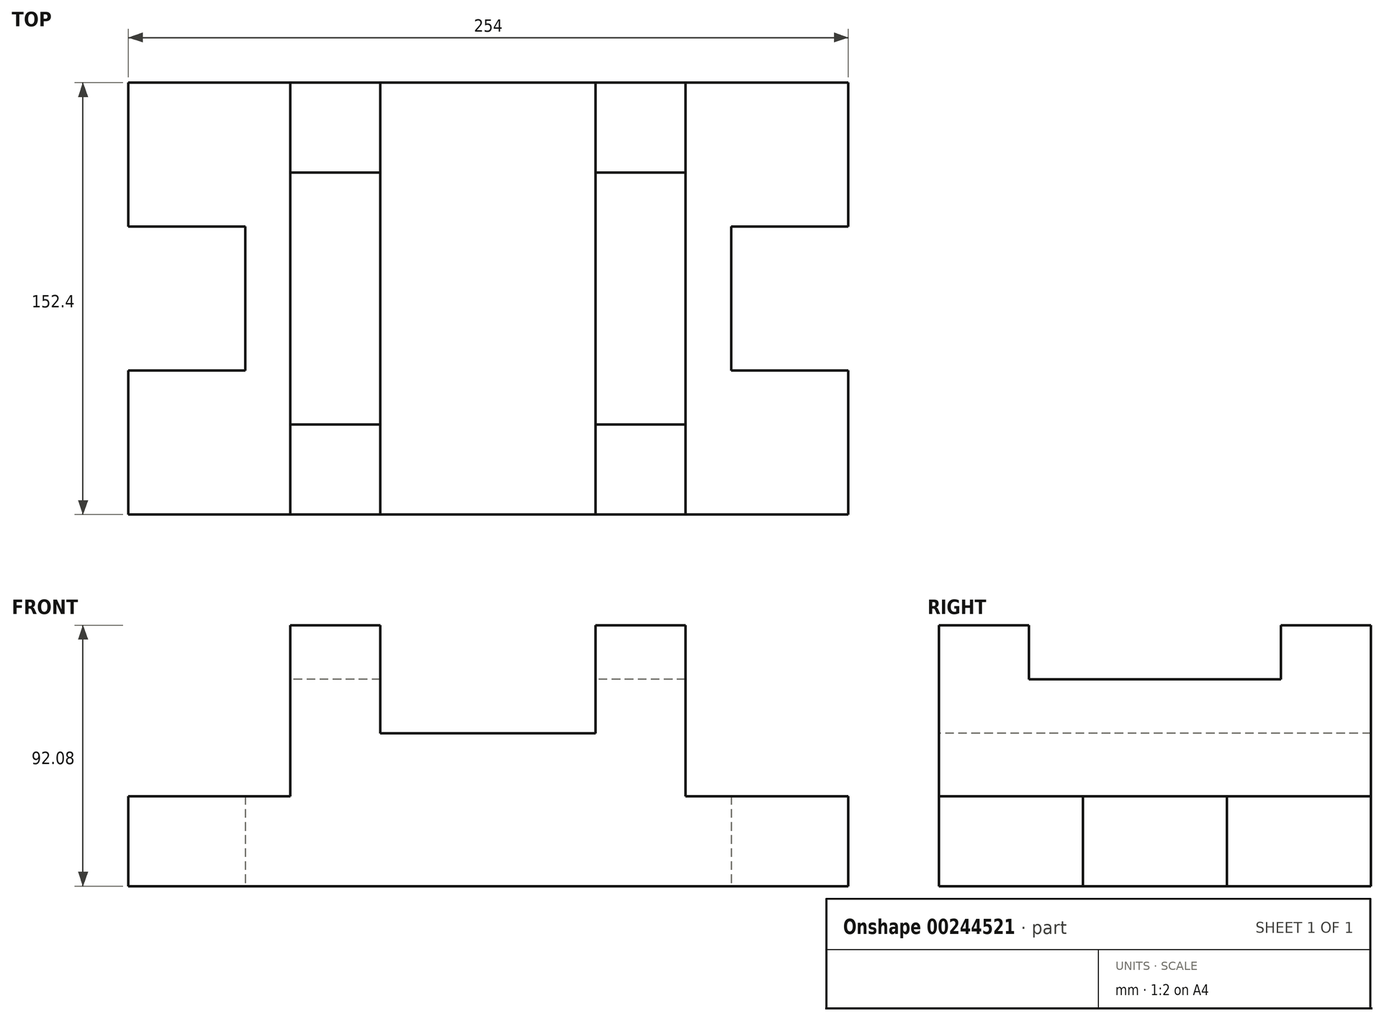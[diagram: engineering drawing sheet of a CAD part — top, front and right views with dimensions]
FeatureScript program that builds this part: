
annotation { "Feature Type Name" : "Feature", "Feature Type Description" : "" }
export const myFeature = defineFeature(function(context is Context, id is Id, definition is map)
    precondition{}
    {
        {
            var Q0;
            Q0=qCreatedBy(makeId("Top.planeOp"),FACE);
            var sketch = newSketch(context, id + "F0", { "sketchPlane" : qUnion([Q0])});
            skLineSegment(sketch, "E0.bottom", {"start": v(127, 76.2) * mm, "end": v(-127, 76.2) * mm});
            skLineSegment(sketch, "E0.top", {"start": v(127, -76.2) * mm, "end": v(-127, -76.2) * mm});
            skLineSegment(sketch, "E0.left", {"start": v(127, 76.2) * mm, "end": v(127, 25.4) * mm});
            skLineSegment(sketch, "E0.right", {"start": v(-127, 76.2) * mm, "end": v(-127, 25.4) * mm});
            skPoint(sketch, "E0.middle", {"position": v(0, 0) * mm});
            skLineSegment(sketch, "E1", {"start": v(-69.85, -76.2) * mm, "end": v(-69.85, 76.2) * mm});
            skLineSegment(sketch, "E2", {"start": v(69.54, -76.2) * mm, "end": v(69.54, 76.2) * mm});
            skLineSegment(sketch, "E3", {"start": v(-38.1, 76.2) * mm, "end": v(-38.1, -76.2) * mm});
            skLineSegment(sketch, "E4", {"start": v(37.8, 76.2) * mm, "end": v(37.8, -76.2) * mm});
            skLineSegment(sketch, "E5", {"start": v(-38.1, 44.45) * mm, "end": v(-69.85, 44.45) * mm});
            skLineSegment(sketch, "E6", {"start": v(69.54, 44.45) * mm, "end": v(37.8, 44.45) * mm});
            skLineSegment(sketch, "E7", {"start": v(-38.1, -44.45) * mm, "end": v(-69.85, -44.45) * mm});
            skLineSegment(sketch, "E8", {"start": v(69.54, -44.45) * mm, "end": v(37.8, -44.45) * mm});
            skPoint(sketch, "E9.middle", {"position": v(-127, 0) * mm});
            skLineSegment(sketch, "E10.right", {"start": v(85.72, 25.4) * mm, "end": v(85.72, -25.4) * mm});
            skPoint(sketch, "E10.middle", {"position": v(127, 0) * mm});
            skLineSegment(sketch, "E11", {"start": v(85.72, -25.4) * mm, "end": v(127, -25.4) * mm});
            skLineSegment(sketch, "E12", {"start": v(85.72, 25.4) * mm, "end": v(127, 25.4) * mm});
            skLineSegment(sketch, "E13.trimOffspring", {"start": v(-127, -25.4) * mm, "end": v(-127, -76.2) * mm});
            skLineSegment(sketch, "E14.trimOffspring", {"start": v(127, -25.4) * mm, "end": v(127, -76.2) * mm});
            skLineSegment(sketch, "E15", {"start": v(-127, -25.4) * mm, "end": v(-85.72, -25.4) * mm});
            skLineSegment(sketch, "E16", {"start": v(-127, 25.4) * mm, "end": v(-85.72, 25.4) * mm});
            skLineSegment(sketch, "E17", {"start": v(-85.72, 25.4) * mm, "end": v(-85.72, -25.4) * mm});
            skSolve(sketch);
        }
        {
            var Q0;
            {var subQ4=sQuery(id+"F0.wireOp",EDGE,"E0.right");Q0=makeQuery(id+"F0.imprint","IMPRINT",FACE,{"disambiguationData":[TD([[makeQuery(id+"F0.imprint","IMPRINT",EDGE,{"derivedFrom":subQ4}),1.0]])]});}
            var Q1;
            {var subQ4=sQuery(id+"F0.wireOp",EDGE,"E0.left");Q1=makeQuery(id+"F0.imprint","IMPRINT",FACE,{"disambiguationData":[TD([[makeQuery(id+"F0.imprint","IMPRINT",EDGE,{"derivedFrom":subQ4}),-1.0]])]});}
            extrude(context, id + "F1", {"entities" : qUnion([Q0, Q1]), "depth" : 31.75 * mm});
        }
        {
            var Q0;
            {var subQ5=sQuery(id+"F0.wireOp",EDGE,"E6");Q0=makeQuery(id+"F0.imprint","IMPRINT",FACE,{"disambiguationData":[TD([[makeQuery(id+"F0.imprint","IMPRINT",EDGE,{"derivedFrom":subQ5}),-1.0]])]});}
            var Q1;
            {var subQ5=sQuery(id+"F0.wireOp",EDGE,"E5");Q1=makeQuery(id+"F0.imprint","IMPRINT",FACE,{"disambiguationData":[TD([[makeQuery(id+"F0.imprint","IMPRINT",EDGE,{"derivedFrom":subQ5}),-1.0]])]});}
            var Q2;
            {var subQ5=sQuery(id+"F0.wireOp",EDGE,"E7");Q2=makeQuery(id+"F0.imprint","IMPRINT",FACE,{"disambiguationData":[TD([[makeQuery(id+"F0.imprint","IMPRINT",EDGE,{"derivedFrom":subQ5}),1.0]])]});}
            var Q3;
            {var subQ5=sQuery(id+"F0.wireOp",EDGE,"E8");Q3=makeQuery(id+"F0.imprint","IMPRINT",FACE,{"disambiguationData":[TD([[makeQuery(id+"F0.imprint","IMPRINT",EDGE,{"derivedFrom":subQ5}),1.0]])]});}
            extrude(context, id + "F2", {"entities" : qUnion([Q0, Q1, Q2, Q3]), "operationType" : NewBodyOperationType.ADD, "depth" : 92.07 * mm});
        }
        {
            var Q0;
            {var subQ0=sQuery(id+"F0.wireOp",EDGE,"E3");var subQ7=sQuery(id+"F0.wireOp",EDGE,"E0.bottom");var subQ8=makeQuery(id+"F0.imprint","INTERSECT",VERTEX,{"derivedFrom":[subQ7,subQ0]});Q0=makeQuery(id+"F0.imprint","IMPRINT",FACE,{"disambiguationData":[TD([[makeQuery(id+"F0.imprint","IMPRINT",EDGE,{"disambiguationData":[TD([[subQ8,1.0]])],"derivedFrom":subQ7}),1.0]])]});}
            extrude(context, id + "F3", {"entities" : qUnion([Q0]), "operationType" : NewBodyOperationType.ADD, "depth" : 53.97 * mm});
        }
        {
            var Q0;
            {var subQ0=sQuery(id+"F0.wireOp",EDGE,"E5");Q0=makeQuery(id+"F0.imprint","IMPRINT",FACE,{"disambiguationData":[TD([[makeQuery(id+"F0.imprint","IMPRINT",EDGE,{"derivedFrom":subQ0}),1.0]])]});}
            var Q1;
            {var subQ0=sQuery(id+"F0.wireOp",EDGE,"E6");Q1=makeQuery(id+"F0.imprint","IMPRINT",FACE,{"disambiguationData":[TD([[makeQuery(id+"F0.imprint","IMPRINT",EDGE,{"derivedFrom":subQ0}),1.0]])]});}
            extrude(context, id + "F4", {"entities" : qUnion([Q0, Q1]), "operationType" : NewBodyOperationType.ADD, "depth" : 73.02 * mm});
        }
    });
